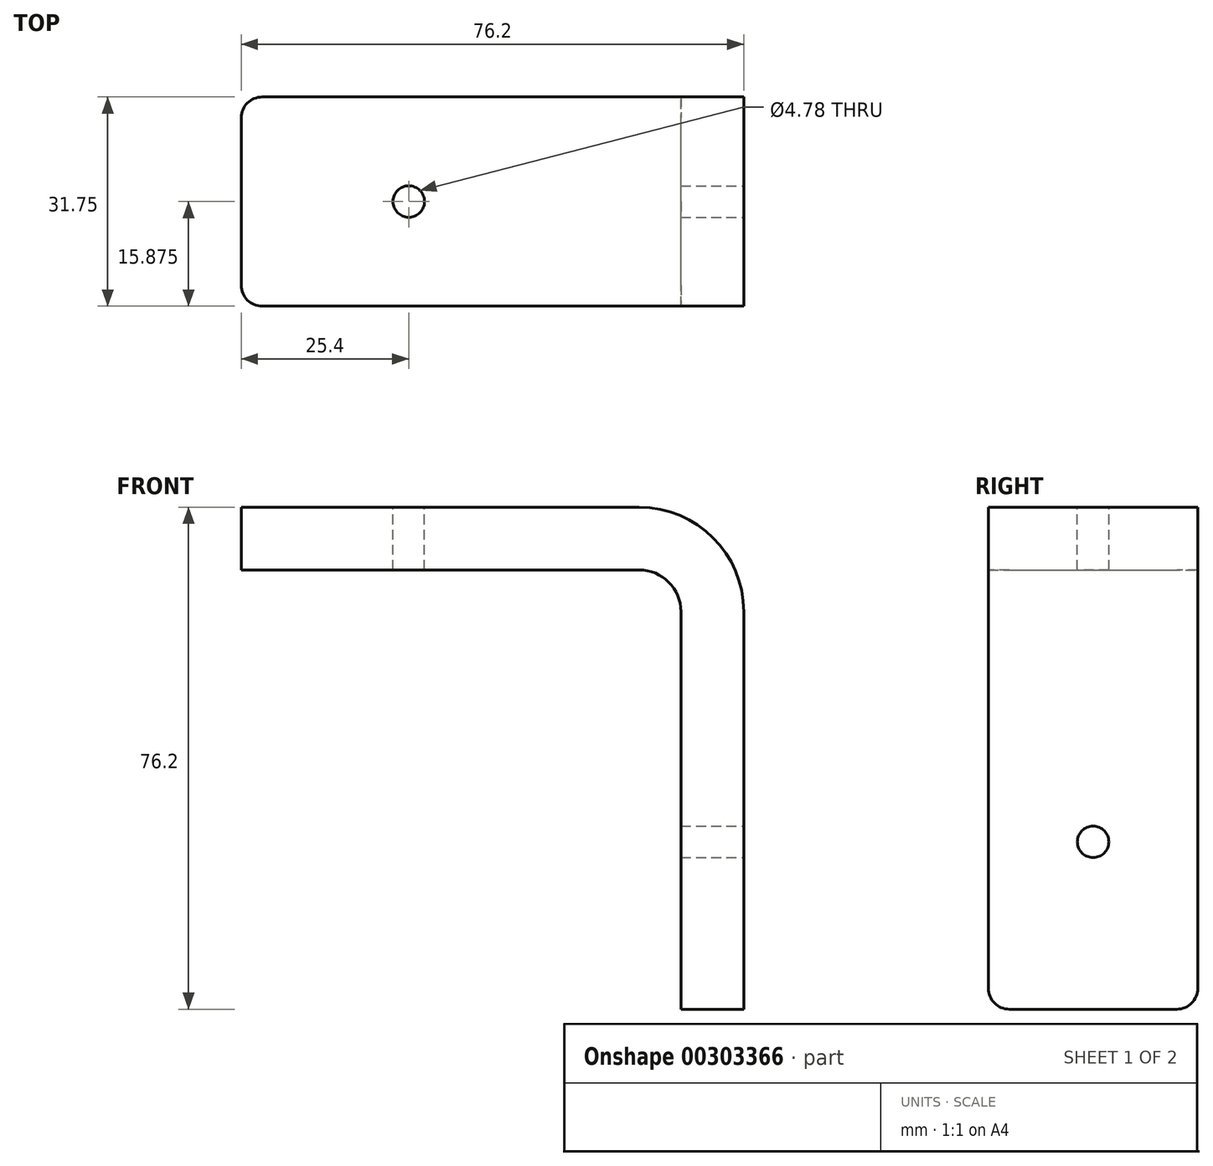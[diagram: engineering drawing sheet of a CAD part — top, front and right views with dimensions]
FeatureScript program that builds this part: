
annotation { "Feature Type Name" : "Feature", "Feature Type Description" : "" }
export const myFeature = defineFeature(function(context is Context, id is Id, definition is map)
    precondition{}
    {
        {
            var Q0;
            Q0=qCreatedBy(makeId("Front.planeOp"),FACE);
            var sketch = newSketch(context, id + "F0", { "sketchPlane" : qUnion([Q0])});
            skLineSegment(sketch, "E0.bottom", {"start": v(0, 0) * mm, "end": v(76.2, 0) * mm});
            skLineSegment(sketch, "E0.top", {"start": v(0, 76.2) * mm, "end": v(76.2, 76.2) * mm});
            skLineSegment(sketch, "E0.left", {"start": v(0, 0) * mm, "end": v(0, 76.2) * mm});
            skLineSegment(sketch, "E0.right", {"start": v(76.2, 0) * mm, "end": v(76.2, 76.2) * mm});
            skLineSegment(sketch, "E1.0", {"start": v(66.67, 0) * mm, "end": v(66.67, 66.67) * mm});
            skLineSegment(sketch, "E1.1", {"start": v(0, 66.67) * mm, "end": v(66.67, 66.67) * mm});
            skSolve(sketch);
        }
        {
            var Q0;
            {var subQ2=sQuery(id+"F0.wireOp",EDGE,"E0.top");Q0=makeQuery(id+"F0.imprint","IMPRINT",FACE,{"disambiguationData":[TD([[makeQuery(id+"F0.imprint","IMPRINT",EDGE,{"derivedFrom":subQ2}),-1.0]])]});}
            extrude(context, id + "F1", {"entities" : qUnion([Q0]), "depth" : 31.75 * mm});
        }
        {
            var Q0;
            Q0=makeQuery(id+"F1.opExtrude","SWEPT_FACE",FACE,{"disambiguationData":[OSD([sQuery(id+"F0.wireOp",EDGE,"E0.right")])]});
            var sketch = newSketch(context, id + "F2", { "sketchPlane" : qUnion([Q0])});
            skCircle(sketch, "E2", {"center": v(-15.88, 25.4) * mm, "radius": 2.39 * mm});
            skPoint(sketch, "E2.centerSnap0", {"position": v(-15.88, 0) * mm});
            skSolve(sketch);
        }
        {
            var Q0;
            Q0=makeQuery(id+"F2.imprint","IMPRINT",FACE,{"disambiguationData":[TD([[makeQuery(id+"F2.imprint","IMPRINT",EDGE,{"derivedFrom":sQuery(id+"F2.wireOp",EDGE,"E2")}),1.0]])]});
            extrude(context, id + "F3", {"entities" : qUnion([Q0]), "operationType" : NewBodyOperationType.REMOVE, "oppositeDirection" : true, "depth" : 25.4 * mm});
        }
        {
            var Q0;
            Q0=makeQuery(id+"F1.opExtrude","SWEPT_FACE",FACE,{"disambiguationData":[OSD([sQuery(id+"F0.wireOp",EDGE,"E0.top")])]});
            var sketch = newSketch(context, id + "F4", { "sketchPlane" : qUnion([Q0])});
            skCircle(sketch, "E3", {"center": v(25.4, -15.87) * mm, "radius": 2.39 * mm});
            skPoint(sketch, "E3.centerSnap0", {"position": v(0, -15.88) * mm});
            skSolve(sketch);
        }
        {
            var Q0;
            Q0=makeQuery(id+"F4.imprint","IMPRINT",FACE,{"disambiguationData":[TD([[makeQuery(id+"F4.imprint","IMPRINT",EDGE,{"derivedFrom":sQuery(id+"F4.wireOp",EDGE,"E3")}),1.0]])]});
            extrude(context, id + "F5", {"entities" : qUnion([Q0]), "operationType" : NewBodyOperationType.REMOVE, "oppositeDirection" : true, "depth" : 25.4 * mm});
        }
        {
            var Q0;
            Q0=makeQuery(id+"F1.opExtrude","SWEPT_EDGE",EDGE,{"disambiguationData":[OSD([sQuery(id+"F0.wireOp",EDGE,"E0.top"),sQuery(id+"F0.wireOp",EDGE,"E0.right")])]});
            fillet(context, id + "F6", {"entities" : qUnion([Q0]), "radius" : 15.88 * mm, "tangentPropagation" : true, "allowEdgeOverflow" : false});
        }
        {
            var Q0;
            Q0=makeQuery(id+"F1.opExtrude","SWEPT_EDGE",EDGE,{"disambiguationData":[OSD([sQuery(id+"F0.wireOp",EDGE,"E1.0"),sQuery(id+"F0.wireOp",EDGE,"E1.1")])]});
            fillet(context, id + "F7", {"entities" : qUnion([Q0]), "radius" : 6.35 * mm, "tangentPropagation" : true, "allowEdgeOverflow" : false});
        }
        {
            var Q0;
            Q0=makeQuery(id+"F1.opExtrude","CAP_EDGE",EDGE,{"disambiguationData":[OSD([sQuery(id+"F0.wireOp",EDGE,"E0.left")])],"isStart":true});
            var Q1;
            Q1=makeQuery(id+"F1.opExtrude","CAP_EDGE",EDGE,{"disambiguationData":[OSD([sQuery(id+"F0.wireOp",EDGE,"E0.left")])],"isStart":false});
            var Q2;
            Q2=makeQuery(id+"F1.opExtrude","CAP_EDGE",EDGE,{"disambiguationData":[OSD([sQuery(id+"F0.wireOp",EDGE,"E0.bottom")])],"isStart":true});
            var Q3;
            Q3=makeQuery(id+"F1.opExtrude","CAP_EDGE",EDGE,{"disambiguationData":[OSD([sQuery(id+"F0.wireOp",EDGE,"E0.bottom")])],"isStart":false});
            fillet(context, id + "F8", {"entities" : qUnion([Q0, Q1, Q2, Q3]), "radius" : 3.17 * mm, "tangentPropagation" : true, "allowEdgeOverflow" : false});
        }
    });
